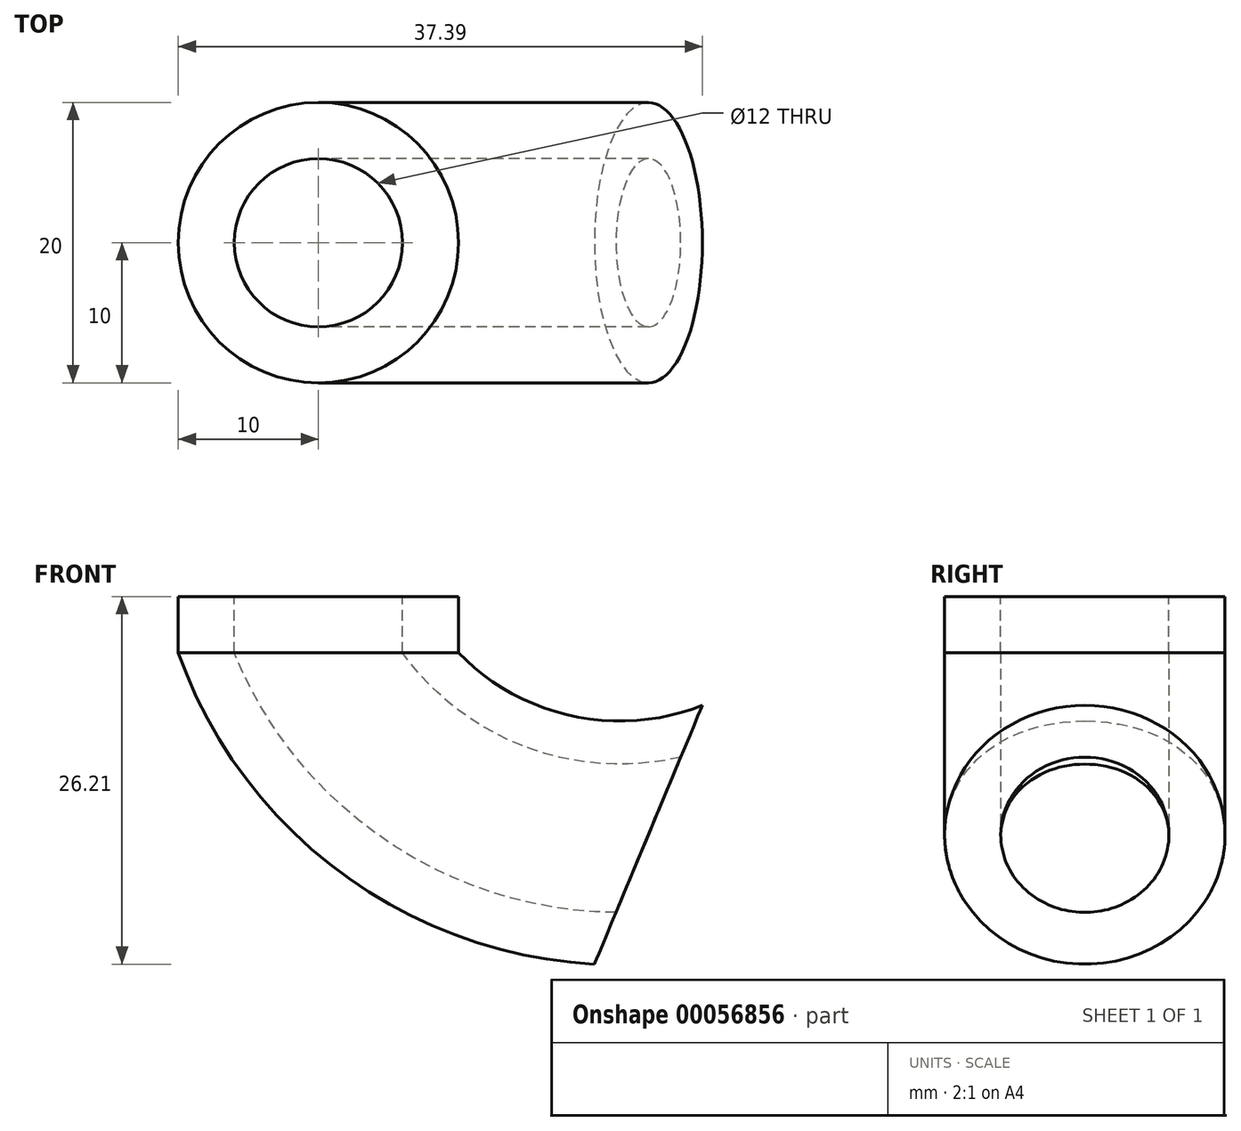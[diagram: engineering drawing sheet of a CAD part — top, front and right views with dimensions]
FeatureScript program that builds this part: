
annotation { "Feature Type Name" : "Feature", "Feature Type Description" : "" }
export const myFeature = defineFeature(function(context is Context, id is Id, definition is map)
    precondition{}
    {
        {
            var Q0;
            Q0=qCreatedBy(makeId("Front.planeOp"),FACE);
            var sketch = newSketch(context, id + "F0", { "sketchPlane" : qUnion([Q0])});
            skLineSegment(sketch, "E0", {"start": v(0, 38.83) * mm, "end": v(0, -7.78) * mm, "construction": true});
            skLineSegment(sketch, "E1.0", {"start": v(-6, 14) * mm, "end": v(-6, 10) * mm, "construction": true});
            skLineSegment(sketch, "E2", {"start": v(-13.36, 0) * mm, "end": v(11.25, 0) * mm, "construction": true});
            skLineSegment(sketch, "E3.0", {"start": v(-13.36, 10) * mm, "end": v(11.25, 10) * mm, "construction": true});
            skLineSegment(sketch, "E4.0", {"start": v(-13.36, 14) * mm, "end": v(11.25, 14) * mm, "construction": true});
            skLineSegment(sketch, "E5.trimOffspring", {"start": v(-6, 0) * mm, "end": v(-6, -7.78) * mm, "construction": true});
            skLineSegment(sketch, "E6.0", {"start": v(-10, 14) * mm, "end": v(-10, 10) * mm, "construction": true});
            skLineSegment(sketch, "E7", {"start": v(-6, 14) * mm, "end": v(-10, 14) * mm});
            skLineSegment(sketch, "E8", {"start": v(-10, 10) * mm, "end": v(-6, 10) * mm});
            skLineSegment(sketch, "E9", {"start": v(-6, 14) * mm, "end": v(-6, 10) * mm});
            skLineSegment(sketch, "E10", {"start": v(-10, 10) * mm, "end": v(-10, 14) * mm});
            skLineSegment(sketch, "E11.0", {"start": v(12, 38.83) * mm, "end": v(12, -7.78) * mm, "construction": true});
            skLineSegment(sketch, "E12.0", {"start": v(-13.36, -5) * mm, "end": v(11.25, -5) * mm, "construction": true});
            skLineSegment(sketch, "E13", {"start": v(12, -5) * mm, "end": v(17.08, -5) * mm});
            skLineSegment(sketch, "E14.0", {"start": v(12, -9) * mm, "end": v(17.08, -9) * mm});
            skLineSegment(sketch, "E15", {"start": v(12, -5) * mm, "end": v(12, -9) * mm});
            skLineSegment(sketch, "E16.0", {"start": v(16, -5) * mm, "end": v(16, -9) * mm});
            skArc(sketch, "E17", {"start": v(0, 10) * mm, "mid": v(5.02, 3.82) * mm, "end": v(12, 0) * mm});
            skLineSegment(sketch, "E18", {"start": v(0, 10) * mm, "end": v(23.54, -2.98) * mm});
            skArc(sketch, "E19", {"start": v(0, 10) * mm, "mid": v(9.8, -0.05) * mm, "end": v(23.54, -2.98) * mm});
            skSolve(sketch);
        }
        {
            var Q0;
            Q0=makeQuery(id+"F0.imprint","IMPRINT",FACE,{"disambiguationData":[TD([[makeQuery(id+"F0.imprint","IMPRINT",EDGE,{"derivedFrom":sQuery(id+"F0.wireOp",EDGE,"E7")}),1.0]])]});
            var Q1;
            Q1=sQuery(id+"F0.wireOp",EDGE,"E0");
            revolve(context, id + "F1", {"entities" : qUnion([Q0]), "axis" : qUnion([Q1]), "revolveType" : RevolveType.FULL});
        }
        {
            var Q0;
            Q0=makeQuery(id+"F1.opRevolve","SWEPT_FACE",FACE,{"disambiguationData":[OSD([sQuery(id+"F0.wireOp",EDGE,"E8")])]});
            var Q1;
            Q1=sQuery(id+"F0.wireOp",EDGE,"E19");
            sweep(context, id + "F2", {"operationType" : NewBodyOperationType.ADD, "profiles" : qUnion([Q0]), "path" : qUnion([Q1])});
        }
    });
